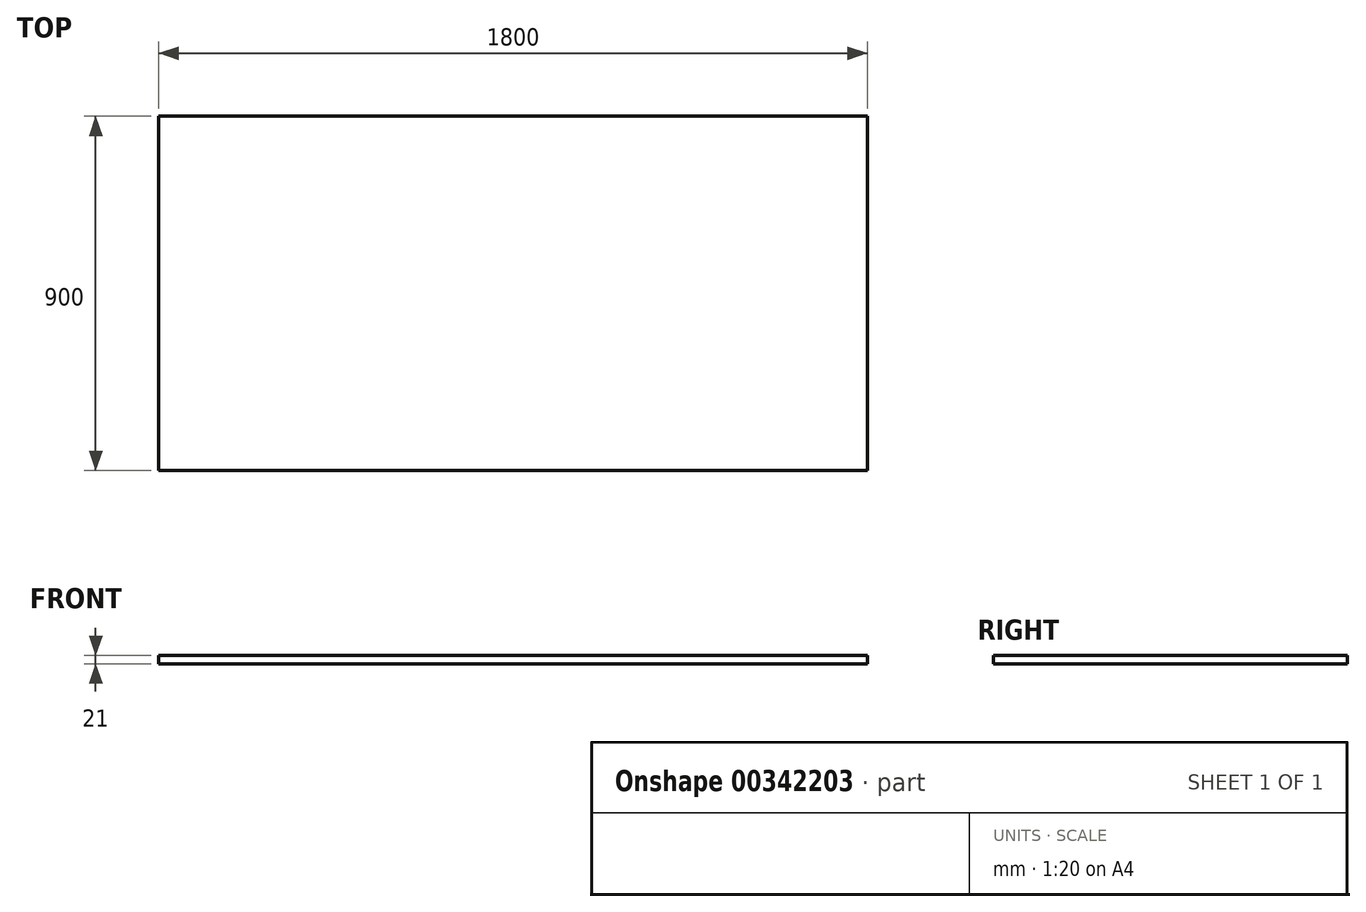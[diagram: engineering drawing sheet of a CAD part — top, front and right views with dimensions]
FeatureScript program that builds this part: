
annotation { "Feature Type Name" : "Feature", "Feature Type Description" : "" }
export const myFeature = defineFeature(function(context is Context, id is Id, definition is map)
    precondition{}
    {
        {
            var Q0;
            Q0=qCreatedBy(makeId("Top.planeOp"),FACE);
            var sketch = newSketch(context, id + "F0", { "sketchPlane" : qUnion([Q0])});
            skLineSegment(sketch, "E0.bottom", {"start": v(-900, 450) * mm, "end": v(900, 450) * mm});
            skLineSegment(sketch, "E0.top", {"start": v(-900, -450) * mm, "end": v(900, -450) * mm});
            skLineSegment(sketch, "E0.left", {"start": v(-900, 450) * mm, "end": v(-900, -450) * mm});
            skLineSegment(sketch, "E0.right", {"start": v(900, 450) * mm, "end": v(900, -450) * mm});
            skPoint(sketch, "E0.middle", {"position": v(0, 0) * mm});
            skSolve(sketch);
        }
        {
            var Q0;
            Q0=makeQuery(id+"F0.imprint","IMPRINT",FACE,{"disambiguationData":[TD([[makeQuery(id+"F0.imprint","IMPRINT",EDGE,{"derivedFrom":sQuery(id+"F0.wireOp",EDGE,"E0.bottom")}),-1.0]])]});
            extrude(context, id + "F1", {"entities" : qUnion([Q0]), "depth" : 21 * mm});
        }
    });
